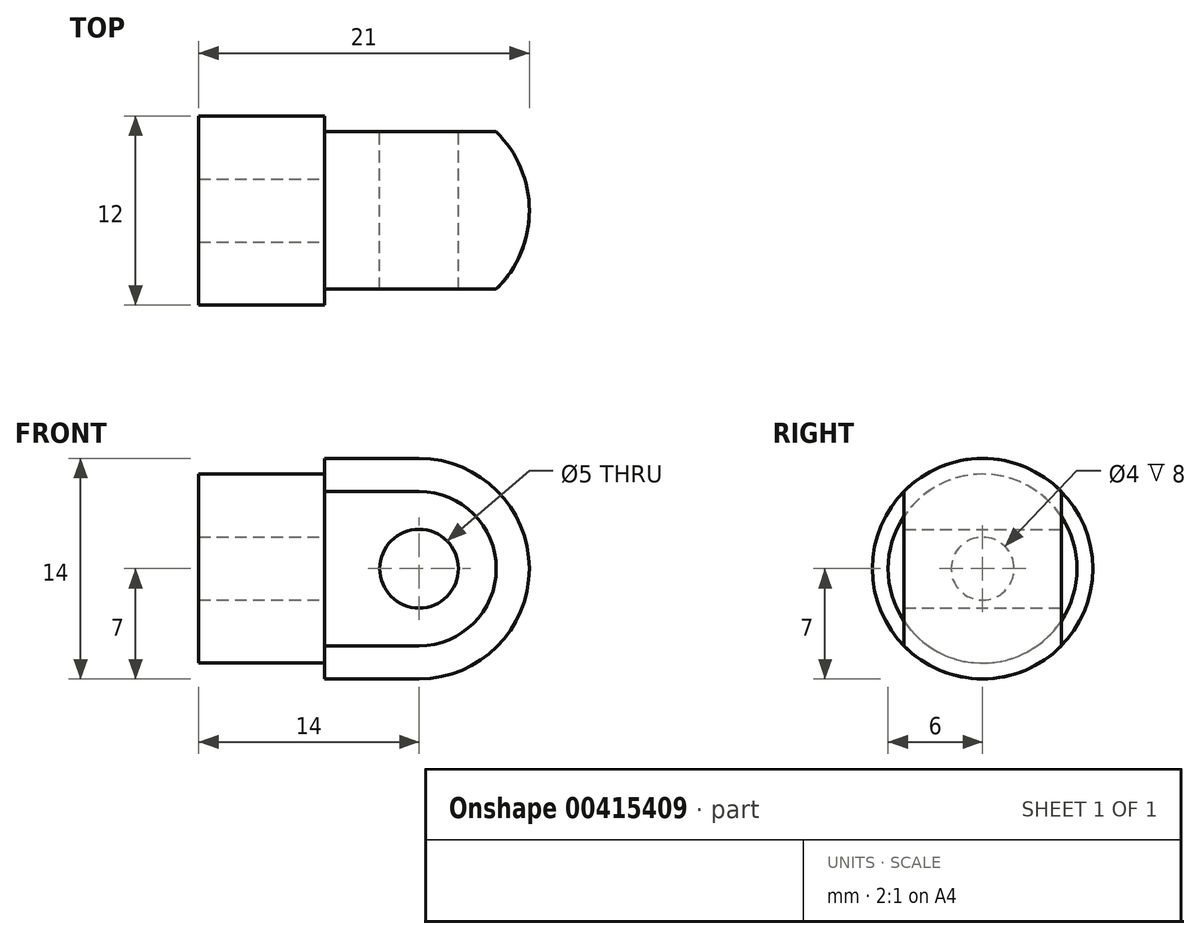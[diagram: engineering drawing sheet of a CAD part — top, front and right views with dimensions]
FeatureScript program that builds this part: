
annotation { "Feature Type Name" : "Feature", "Feature Type Description" : "" }
export const myFeature = defineFeature(function(context is Context, id is Id, definition is map)
    precondition{}
    {
        {
            var Q0;
            Q0=qCreatedBy(makeId("Top.planeOp"),FACE);
            var sketch = newSketch(context, id + "F0", { "sketchPlane" : qUnion([Q0])});
            skLineSegment(sketch, "E0", {"start": v(0, 0) * mm, "end": v(0, 6) * mm});
            skLineSegment(sketch, "E1", {"start": v(0, 6) * mm, "end": v(8, 6) * mm});
            skLineSegment(sketch, "E2", {"start": v(8, 6) * mm, "end": v(8, 7) * mm});
            skLineSegment(sketch, "E3", {"start": v(0, 0) * mm, "end": v(-9.54, 0) * mm, "construction": true});
            skLineSegment(sketch, "E4", {"start": v(8, 0) * mm, "end": v(21, 0) * mm});
            skLineSegment(sketch, "E5", {"start": v(8, 7) * mm, "end": v(14, 7) * mm});
            skLineSegment(sketch, "E6", {"start": v(21, 0) * mm, "end": v(21, 0) * mm});
            skPoint(sketch, "E7.visualSharp", {"position": v(21, 7) * mm});
            skArc(sketch, "E7.filletArc", {"start": v(21, 0) * mm, "mid": v(18.95, 4.95) * mm, "end": v(14, 7) * mm});
            skLineSegment(sketch, "E8", {"start": v(0, 2) * mm, "end": v(8, 2) * mm});
            skLineSegment(sketch, "E9", {"start": v(8, 2) * mm, "end": v(8, 0) * mm});
            skPoint(sketch, "E10.orphan", {"position": v(6.51, 0) * mm});
            skSolve(sketch);
        }
        {
            var Q0;
            Q0=makeQuery(id+"F0.imprint","IMPRINT",FACE,{"disambiguationData":[TD([[makeQuery(id+"F0.imprint","IMPRINT",EDGE,{"derivedFrom":sQuery(id+"F0.wireOp",EDGE,"E0")}),-1.0]])]});
            var Q1;
            Q1=sQuery(id+"F0.wireOp",EDGE,"E3");
            revolve(context, id + "F1", {"entities" : qUnion([Q0]), "axis" : qUnion([Q1]), "revolveType" : RevolveType.FULL});
        }
        {
            var Q0;
            Q0=qCreatedBy(makeId("Top.planeOp"),FACE);
            var sketch = newSketch(context, id + "F2", { "sketchPlane" : qUnion([Q0])});
            skLineSegment(sketch, "E11", {"start": v(0, 0) * mm, "end": v(37.67, 0) * mm, "construction": true});
            skLineSegment(sketch, "E12", {"start": v(28, -5) * mm, "end": v(8, -5) * mm});
            skLineSegment(sketch, "E13", {"start": v(8, -5) * mm, "end": v(8, -13.81) * mm});
            skLineSegment(sketch, "E14", {"start": v(8, -13.81) * mm, "end": v(28, -13.81) * mm});
            skLineSegment(sketch, "E15", {"start": v(28, -13.81) * mm, "end": v(28, -5) * mm});
            skLineSegment(sketch, "E16.MirrorCS", {"start": v(28, 13.81) * mm, "end": v(28, 5) * mm});
            skLineSegment(sketch, "E17.MirrorCS", {"start": v(8, 13.81) * mm, "end": v(28, 13.81) * mm});
            skLineSegment(sketch, "E18.MirrorCS", {"start": v(8, 5) * mm, "end": v(8, 13.81) * mm});
            skLineSegment(sketch, "E19.MirrorCS", {"start": v(28, 5) * mm, "end": v(8, 5) * mm});
            skSolve(sketch);
        }
        {
            var Q0;
            Q0 = qSketchRegion(id + "F2", true);
            extrude(context, id + "F3", {"entities" : qUnion([Q0]), "operationType" : NewBodyOperationType.REMOVE, "endBound" : BoundingType.SYMMETRIC, "oppositeDirection" : true, "depth" : 25 * mm});
        }
        {
            var Q0;
            Q0=makeQuery(id+"F3.boolean.opBoolean","COPY",FACE,{"derivedFrom":makeQuery(id+"F3.opExtrude","SWEPT_FACE",FACE,{"disambiguationData":[OSD([sQuery(id+"F2.wireOp",EDGE,"E19.MirrorCS")])]})});
            var sketch = newSketch(context, id + "F4", { "sketchPlane" : qUnion([Q0])});
            skCircle(sketch, "E20", {"center": v(-14, 0) * mm, "radius": 2.5 * mm});
            skSolve(sketch);
        }
        {
            var Q0;
            Q0=makeQuery(id+"F4.imprint","IMPRINT",FACE,{"disambiguationData":[TD([[makeQuery(id+"F4.imprint","IMPRINT",EDGE,{"derivedFrom":sQuery(id+"F4.wireOp",EDGE,"E20")}),1.0]])]});
            extrude(context, id + "F5", {"entities" : qUnion([Q0]), "operationType" : NewBodyOperationType.REMOVE, "oppositeDirection" : true, "depth" : 25 * mm});
        }
    });
